# Revit family: Sanitary_Other-Sanitary_AXOR_39001XXX-AXOR-Citterio-Single-lever-basi_
name_source: partatom
category: Plumbing Fixtures
revit_build: Autodesk Revit 2018 (Build: 20170223_1515(x64)
units: mm (PartAtom-declared; Revit-internal decimal feet)

## family parameters
Always vertical = No
Cut with Voids When Loaded = No
OmniClass Number = 23.40.20.00
OmniClass Title = General Furniture and Specialties
Part Type = Normal
Room Calculation Point = No
Round Connector Dimension = Use Diameter
Shared = No
Work Plane-Based = No

## types (16) — shared parameters
Always visible = Yes
BIMobject category = Other Sanitary
Design country = Germany
EAN code = 4059625358030
Edition number = 1
GTIN code = https://4059625358030
IFC Classification = Sanitary Terminal
Installation instructions = https://www.axor-design.com
Manufacturer country = Germany
Manufacturer name = AXOR
Material main = Chrome
Product Guid = 93f47045-00ad-497d-846d-8d3352a25a4a
Product SKU = 39001XXX
Product data url = https://www.bimobject.com
Product family = AXOR Citterio
Product group = Basin mixers
Product name = 39001XXX AXOR Citterio Single lever basin mixer 90 with lever handle for hand washbasins with pop-up waste set - rhombic cut
Product url = https://www.axor-design.com
QR code = https://www.bimobject.com
Technical description = https://www.axor-design.com

## per-type parameters (varying)
| type | Material 1 |
| 000 Chrome | AXOR - AXOR Citterio - 000 Chrome |
| 340 Brushed Black Chrome | AXOR - AXOR Citterio - 340 Brushed Black Chrome |
| 950 Brushed Brass | AXOR - AXOR Citterio - 950 Brushed Brass |
| 140 Brushed Bronze | AXOR - AXOR Citterio - 140 Brushed Bronze |
| 260 Brushed Chrome | AXOR - AXOR Citterio - 260 Brushed Chrome |
| 250 Brushed Gold Optic | AXOR - AXOR Citterio - 250 Brushed Gold Optic |
| 820 Brushed Nickel | AXOR - AXOR Citterio - 820 Brushed Nickel |
| 310 Brushed Red Gold | AXOR - AXOR Citterio - 310 Brushed Red Gold |
| 330 Polished Black Chrome | AXOR - AXOR Citterio - 330 Polished Black Chrome |
| 930 Polished Brass | AXOR - AXOR Citterio - 930 Polished Brass |
| 130 Polished Bronze | AXOR - AXOR Citterio - 130 Polished Bronze |
| 020 Polished Chrome | AXOR - AXOR Citterio - 020 Polished Chrome |
| 990 Polished Gold Optic | AXOR - AXOR Citterio - 990 Polished Gold Optic |
| 830 Polished Nickel | AXOR - AXOR Citterio - 830 Polished Nickel |
| 300 Polished Red Gold | AXOR - AXOR Citterio - 300 Polished Red Gold |
| 800 Stainless Steel Optic | AXOR - AXOR Citterio - 800 Stainless Steel Optic |

## geometry (parser evidence)
native form markers: Sweep x3
no freeform markers — native parametric forms only
